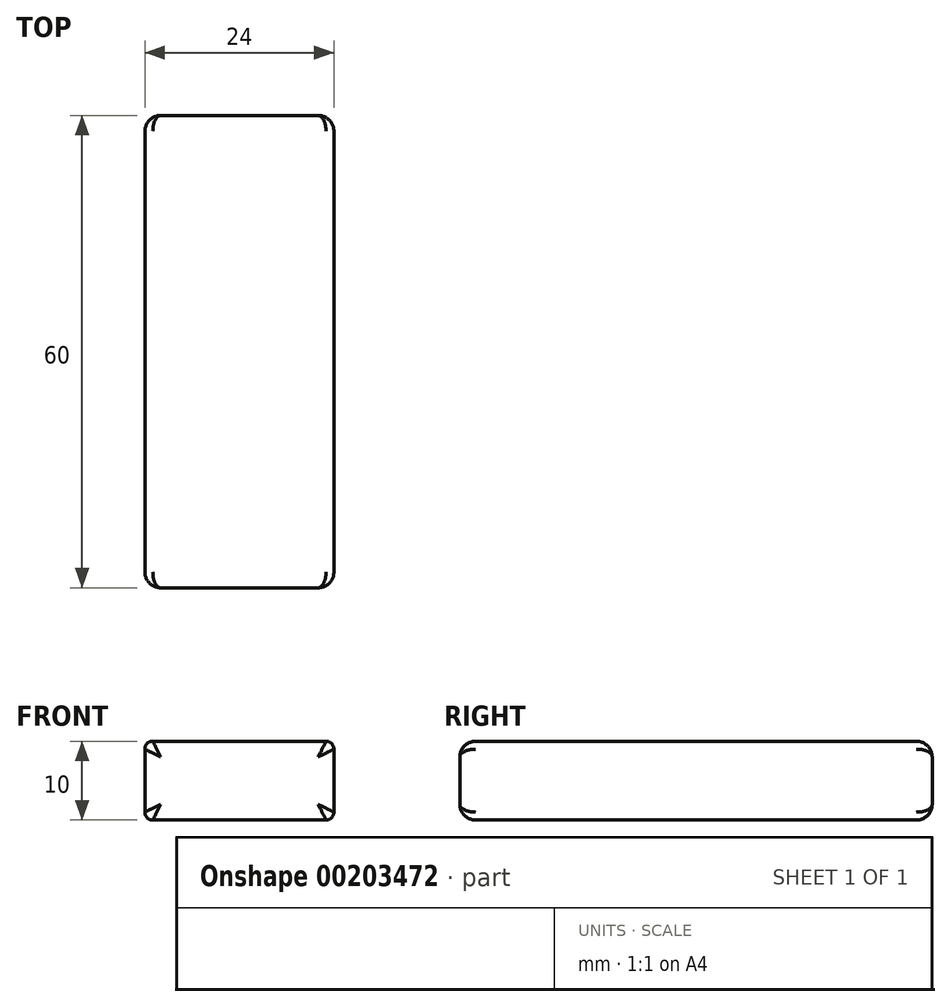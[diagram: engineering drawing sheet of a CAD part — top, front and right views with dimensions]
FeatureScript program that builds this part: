
annotation { "Feature Type Name" : "Feature", "Feature Type Description" : "" }
export const myFeature = defineFeature(function(context is Context, id is Id, definition is map)
    precondition{}
    {
        {
            var Q0;
            Q0=qCreatedBy(makeId("Top.planeOp"),FACE);
            var sketch = newSketch(context, id + "F0", { "sketchPlane" : qUnion([Q0])});
            skLineSegment(sketch, "E0.bottom", {"start": v(12, 30) * mm, "end": v(-12, 30) * mm});
            skLineSegment(sketch, "E0.top", {"start": v(12, -30) * mm, "end": v(-12, -30) * mm});
            skLineSegment(sketch, "E0.left", {"start": v(12, 30) * mm, "end": v(12, -30) * mm});
            skLineSegment(sketch, "E0.right", {"start": v(-12, 30) * mm, "end": v(-12, -30) * mm});
            skPoint(sketch, "E0.middle", {"position": v(0, 0) * mm});
            skSolve(sketch);
        }
        {
            var Q0;
            Q0=makeQuery(id+"F0.imprint","IMPRINT",FACE,{"disambiguationData":[TD([[makeQuery(id+"F0.imprint","IMPRINT",EDGE,{"derivedFrom":sQuery(id+"F0.wireOp",EDGE,"E0.bottom")}),1.0]])]});
            extrude(context, id + "F1", {"entities" : qUnion([Q0]), "depth" : 10 * mm});
        }
        {
            var Q0;
            Q0=makeQuery(id+"F1.opExtrude","CAP_EDGE",EDGE,{"disambiguationData":[OSD([sQuery(id+"F0.wireOp",EDGE,"E0.right")])],"isStart":false});
            var Q1;
            Q1=makeQuery(id+"F1.opExtrude","CAP_EDGE",EDGE,{"disambiguationData":[OSD([sQuery(id+"F0.wireOp",EDGE,"E0.right")])],"isStart":true});
            var Q2;
            Q2=makeQuery(id+"F1.opExtrude","CAP_EDGE",EDGE,{"disambiguationData":[OSD([sQuery(id+"F0.wireOp",EDGE,"E0.left")])],"isStart":false});
            var Q3;
            Q3=makeQuery(id+"F1.opExtrude","CAP_EDGE",EDGE,{"disambiguationData":[OSD([sQuery(id+"F0.wireOp",EDGE,"E0.left")])],"isStart":true});
            fillet(context, id + "F2", {"entities" : qUnion([Q0, Q1, Q2, Q3]), "radius" : 1 * mm, "tangentPropagation" : true, "allowEdgeOverflow" : false});
        }
        {
            var Q0;
            Q0=makeQuery(id+"F1.opExtrude","CAP_EDGE",EDGE,{"disambiguationData":[OSD([sQuery(id+"F0.wireOp",EDGE,"E0.top")])],"isStart":false});
            var Q1;
            Q1=makeQuery(id+"F1.opExtrude","CAP_EDGE",EDGE,{"disambiguationData":[OSD([sQuery(id+"F0.wireOp",EDGE,"E0.top")])],"isStart":true});
            var Q2;
            Q2=makeQuery(id+"F1.opExtrude","SWEPT_EDGE",EDGE,{"disambiguationData":[OSD([sQuery(id+"F0.wireOp",EDGE,"E0.top"),sQuery(id+"F0.wireOp",EDGE,"E0.right")])]});
            var Q3;
            Q3=makeQuery(id+"F1.opExtrude","SWEPT_EDGE",EDGE,{"disambiguationData":[OSD([sQuery(id+"F0.wireOp",EDGE,"E0.top"),sQuery(id+"F0.wireOp",EDGE,"E0.left")])]});
            var Q4;
            Q4=makeQuery(id+"F1.opExtrude","SWEPT_FACE",FACE,{"disambiguationData":[OSD([sQuery(id+"F0.wireOp",EDGE,"E0.bottom")])]});
            fillet(context, id + "F3", {"entities" : qUnion([Q0, Q1, Q2, Q3, Q4]), "radius" : 2 * mm, "allowEdgeOverflow" : false});
        }
    });
